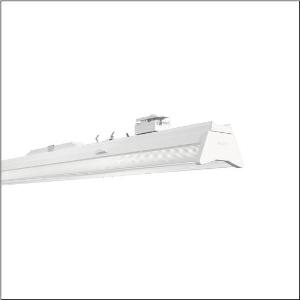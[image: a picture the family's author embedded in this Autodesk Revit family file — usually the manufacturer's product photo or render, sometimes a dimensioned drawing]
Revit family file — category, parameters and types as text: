
# Revit family: licross_r__21_performance_mo_52tm167n485g_c234
name_source: partatom
category: Lighting Fixtures
units: mm (PartAtom-declared; Revit-internal decimal feet)

## family parameters
Cut with Voids When Loaded = No
Host = Face
Light Source = No
Part Type = Normal
Room Calculation Point = No
Round Connector Dimension = Use Diameter
Shared = No

## types (1)
- Licross® 21 Performance MO (1 x LED, 8720 lm, 47.9 W, 4000K)
    Apparent Load = 48 VA
    CIE Flux Codes = 66 88 96 79 100
    Color Rendering = 80
    Color Temperature = 4000K
    Default Elevation = 1800 mm
    Description = Licross® 21 Performance MO, luminaire insert, of sheet steel, galvanised, coil coated, white, length: 1.500mm, width: 120mm, height: 123mm, LED rated luminous flux: 8.720lm, light colour: 840, control gear: ON/OFF, with plug, 3-pole, with phase selection, mains connection: 220..240V, AC, 50/60Hz, rated input power: 48W, halogen-free wiring, primary light control with lens, of plastic, primary optical cover: cover, of PMMA, light emission: direct/indirect distribution, primary light characteristic: symmetric, protection rating (complete): IP40, insulation class (complete): insulation class I (protective earthing), certification: CE, ENEC, UKCA, protection symbol: D if used in an environment without relevant dust loads with corresponding accessories, impact resistance: IK06, permissible ambient temperature for indoor applications: -35..+45°C, corresponds to IFS (International Featured Standards) requirements for safety and quality in the food industry, reducing of maximum allowable ambient temperature of 5°C with ceiling mounting, LABS conformity tested according to VDMA 24364:2018-05, packaging unit: 1 piece
    Height = 114 mm
    Lamp = 1 x LED
    Lamp Light Flux = 8720 lm
    Lamp Power = 47.9 W
    Lamp count = 1
    Length = 1500 mm
    Luminous efficacy = 182 lm/W
    Manufacturer = Siteco
    ModVariant = No
    Model = 52TM167N485G
    Mounting Place = Ceiling
    Mounting Type = Pendant
    Number of Poles = 1
    OnlyDefault = Yes
    Power Factor = 1
    Product Name = Licross® 21 Performance MO
    Product group = luminaire insert
    ProductGroupID = 901
    Protection Class = Protection class I
    Protection Degree = IP 40
    RLX_Detail_Level = 1
    RLX_Emergency_Light_Flux = 0 lm
    RLX_Emergency_Type = 0
    RLX_Emergency_Type_DB = No
    RlxData = <blob elided: 30377 chars, md5=32f508f3>
    Socket = socket
    Standby Power = 0 W
    System Light Flux = 8720 lm
    System Power = 48 W
    Type Comments = Product without accessories
    Type Image = l_1256138.jpg
    URL = http://relux.com
    VarID = ---
    Voltage = 0 V
    Weight = 0.00 kg
    Width = 120 mm

## geometry (parser evidence)
native form markers: Blend x4, Sweep x13
no freeform markers — native parametric forms only
